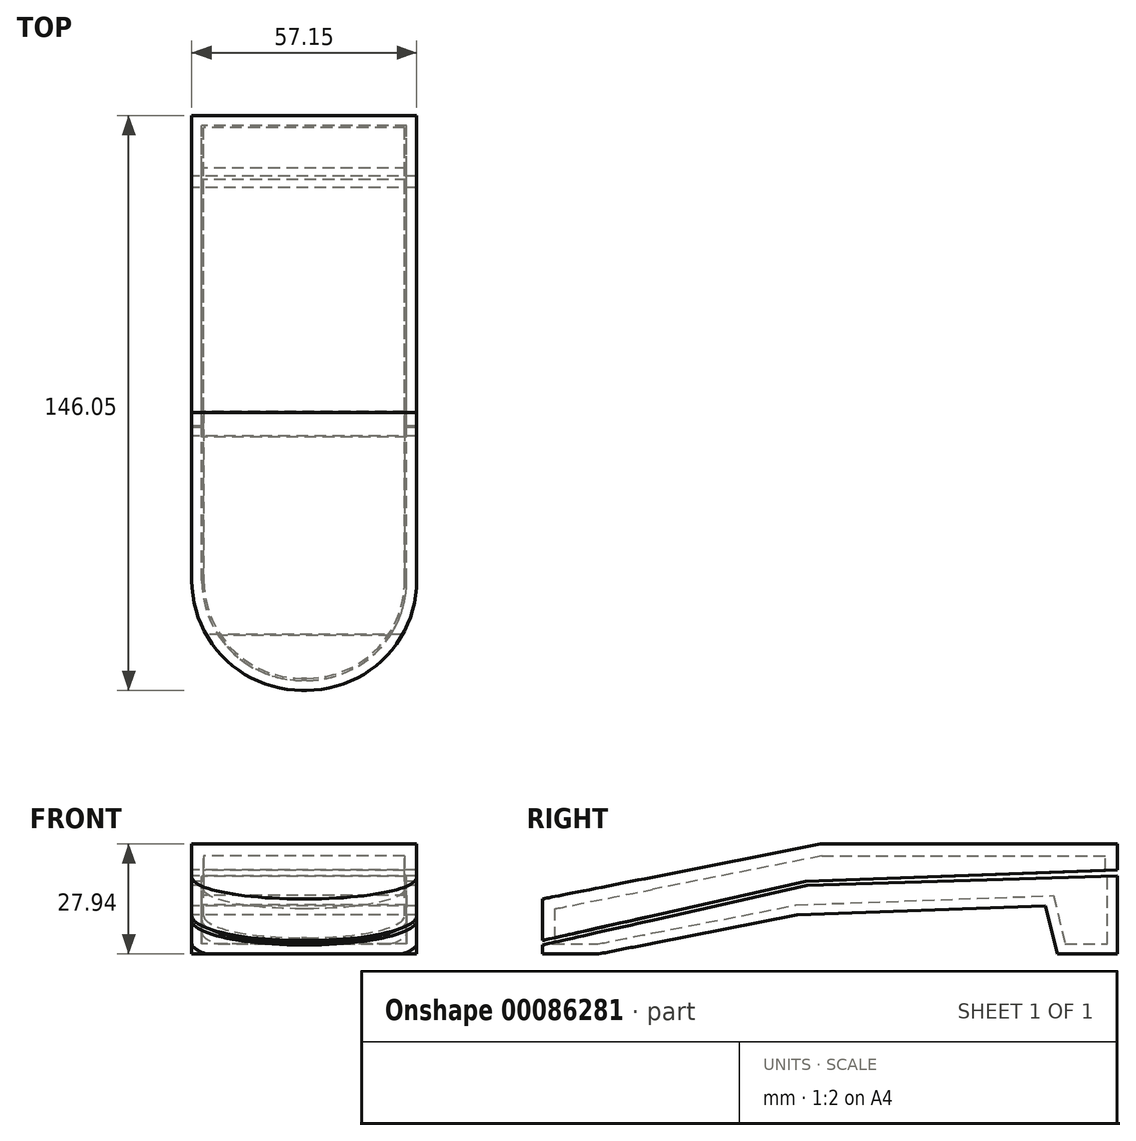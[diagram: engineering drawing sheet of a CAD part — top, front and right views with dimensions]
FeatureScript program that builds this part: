
annotation { "Feature Type Name" : "Feature", "Feature Type Description" : "" }
export const myFeature = defineFeature(function(context is Context, id is Id, definition is map)
    precondition{}
    {
        {
            var Q0;
            Q0=qCreatedBy(makeId("Right.planeOp"),FACE);
            var sketch = newSketch(context, id + "F0", { "sketchPlane" : qUnion([Q0])});
            skLineSegment(sketch, "E0.bottom", {"start": v(-73.12, 0) * mm, "end": v(72.93, 0) * mm});
            skLineSegment(sketch, "E0.top", {"start": v(-73.12, 27.94) * mm, "end": v(72.93, 27.94) * mm});
            skLineSegment(sketch, "E0.left", {"start": v(-73.12, 0) * mm, "end": v(-73.12, 27.94) * mm});
            skLineSegment(sketch, "E0.right", {"start": v(72.93, 0) * mm, "end": v(72.93, 27.94) * mm});
            skLineSegment(sketch, "E1", {"start": v(-2.5, 27.94) * mm, "end": v(-73.12, 13.97) * mm});
            skLineSegment(sketch, "E2", {"start": v(-58.9, 0) * mm, "end": v(-8.49, 9.9) * mm});
            skLineSegment(sketch, "E3", {"start": v(-8.49, 9.9) * mm, "end": v(54.65, 12.2) * mm});
            skLineSegment(sketch, "E4", {"start": v(54.65, 12.2) * mm, "end": v(57.58, 0) * mm});
            skLineSegment(sketch, "E5", {"start": v(-73.12, 3.41) * mm, "end": v(-6.32, 18.43) * mm});
            skLineSegment(sketch, "E6", {"start": v(-6.32, 18.43) * mm, "end": v(72.93, 21.36) * mm});
            skLineSegment(sketch, "E7", {"start": v(-73.12, 2.3) * mm, "end": v(-5.98, 17.4) * mm});
            skLineSegment(sketch, "E8", {"start": v(-5.98, 17.4) * mm, "end": v(72.93, 19.81) * mm});
            skSolve(sketch);
        }
        {
            var Q0;
            {var subQ0=sQuery(id+"F0.wireOp",EDGE,"E1");Q0=makeQuery(id+"F0.imprint","IMPRINT",FACE,{"disambiguationData":[TD([[makeQuery(id+"F0.imprint","IMPRINT",EDGE,{"derivedFrom":subQ0}),1.0]])]});}
            extrude(context, id + "F1", {"entities" : qUnion([Q0]), "depth" : 57.15 * mm});
        }
        {
            var Q0;
            Q0=makeQuery(id+"F1.opExtrude","CAP_EDGE",EDGE,{"disambiguationData":[OSD([sQuery(id+"F0.wireOp",EDGE,"E0.left")])],"isStart":true});
            var Q1;
            Q1=makeQuery(id+"F1.opExtrude","CAP_EDGE",EDGE,{"disambiguationData":[OSD([sQuery(id+"F0.wireOp",EDGE,"E0.left")])],"isStart":false});
            fillet(context, id + "F2", {"entities" : qUnion([Q0, Q1]), "radius" : 27.94 * mm, "tangentPropagation" : true, "allowEdgeOverflow" : false});
        }
        {
            var Q0;
            Q0=makeQuery(id+"F1.opExtrude","SWEPT_FACE",FACE,{"disambiguationData":[OSD([sQuery(id+"F0.wireOp",EDGE,"E6")])]});
            var Q1;
            Q1=makeQuery(id+"F1.opExtrude","SWEPT_FACE",FACE,{"disambiguationData":[OSD([sQuery(id+"F0.wireOp",EDGE,"E5")])]});
            shell(context, id + "F3", {"entities" : qUnion([Q0, Q1]), "thickness" : 3.05 * mm});
        }
        {
            var Q0;
            {var subQ8=sQuery(id+"F0.wireOp",EDGE,"E2");Q0=makeQuery(id+"F0.imprint","IMPRINT",FACE,{"disambiguationData":[TD([[makeQuery(id+"F0.imprint","IMPRINT",EDGE,{"derivedFrom":subQ8}),1.0]])]});}
            extrude(context, id + "F4", {"entities" : qUnion([Q0]), "depth" : 57.15 * mm});
        }
        {
            var Q0;
            Q0=makeQuery(id+"F4.opExtrude","CAP_EDGE",EDGE,{"disambiguationData":[OSD([sQuery(id+"F0.wireOp",EDGE,"E0.left")])],"isStart":false});
            var Q1;
            Q1=makeQuery(id+"F4.opExtrude","CAP_EDGE",EDGE,{"disambiguationData":[OSD([sQuery(id+"F0.wireOp",EDGE,"E0.left")])],"isStart":true});
            fillet(context, id + "F5", {"entities" : qUnion([Q0, Q1]), "radius" : 27.94 * mm, "tangentPropagation" : true, "allowEdgeOverflow" : false});
        }
        {
            var Q0;
            Q0=makeQuery(id+"F4.opExtrude","SWEPT_FACE",FACE,{"disambiguationData":[OSD([sQuery(id+"F0.wireOp",EDGE,"E7")])]});
            var Q1;
            Q1=makeQuery(id+"F4.opExtrude","SWEPT_FACE",FACE,{"disambiguationData":[OSD([sQuery(id+"F0.wireOp",EDGE,"E8")])]});
            shell(context, id + "F6", {"entities" : qUnion([Q0, Q1]), "thickness" : 2.54 * mm});
        }
    });
